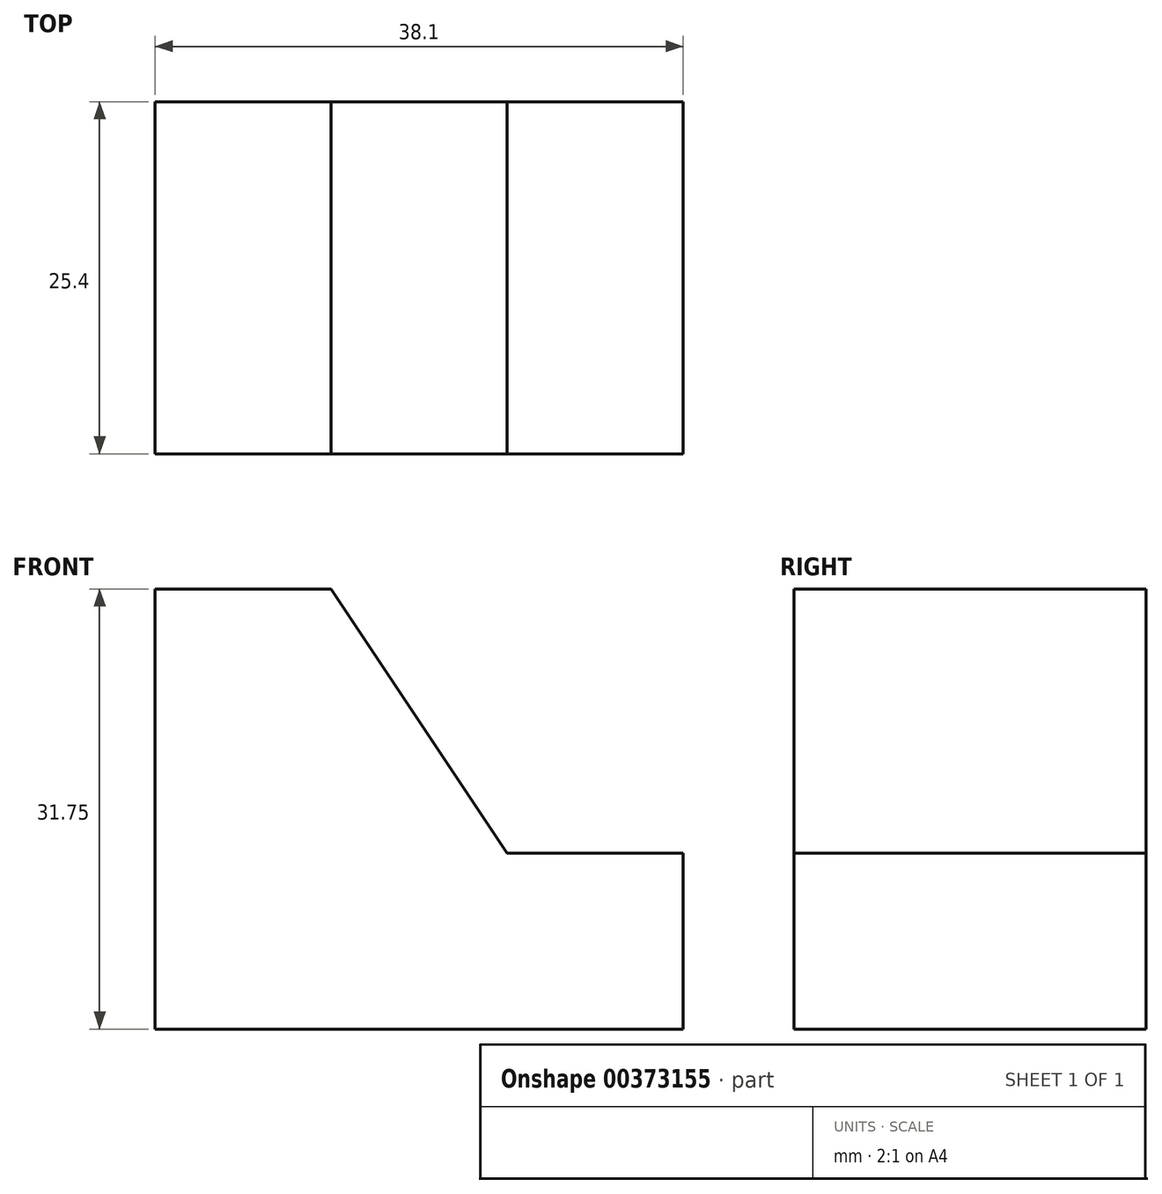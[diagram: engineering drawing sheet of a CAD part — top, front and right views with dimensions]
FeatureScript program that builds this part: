
annotation { "Feature Type Name" : "Feature", "Feature Type Description" : "" }
export const myFeature = defineFeature(function(context is Context, id is Id, definition is map)
    precondition{}
    {
        {
            var Q0;
            Q0=qCreatedBy(makeId("Front.planeOp"),FACE);
            var sketch = newSketch(context, id + "F0", { "sketchPlane" : qUnion([Q0])});
            skLineSegment(sketch, "E0", {"start": v(0, 0) * mm, "end": v(0, 31.75) * mm});
            skLineSegment(sketch, "E1", {"start": v(0, 31.75) * mm, "end": v(12.7, 31.75) * mm});
            skLineSegment(sketch, "E2", {"start": v(12.7, 31.75) * mm, "end": v(12.7, 12.7) * mm});
            skLineSegment(sketch, "E3", {"start": v(0, 0) * mm, "end": v(38.1, 0) * mm});
            skLineSegment(sketch, "E4", {"start": v(38.1, 0) * mm, "end": v(38.1, 12.7) * mm});
            skLineSegment(sketch, "E5", {"start": v(38.1, 12.7) * mm, "end": v(25.4, 12.7) * mm});
            skLineSegment(sketch, "E6", {"start": v(25.4, 12.7) * mm, "end": v(12.7, 31.75) * mm});
            skSolve(sketch);
        }
        {
            var Q0;
            Q0 = qSketchRegion(id + "F0", true);
            extrude(context, id + "F1", {"entities" : qUnion([Q0]), "depth" : 25.4 * mm});
        }
    });
